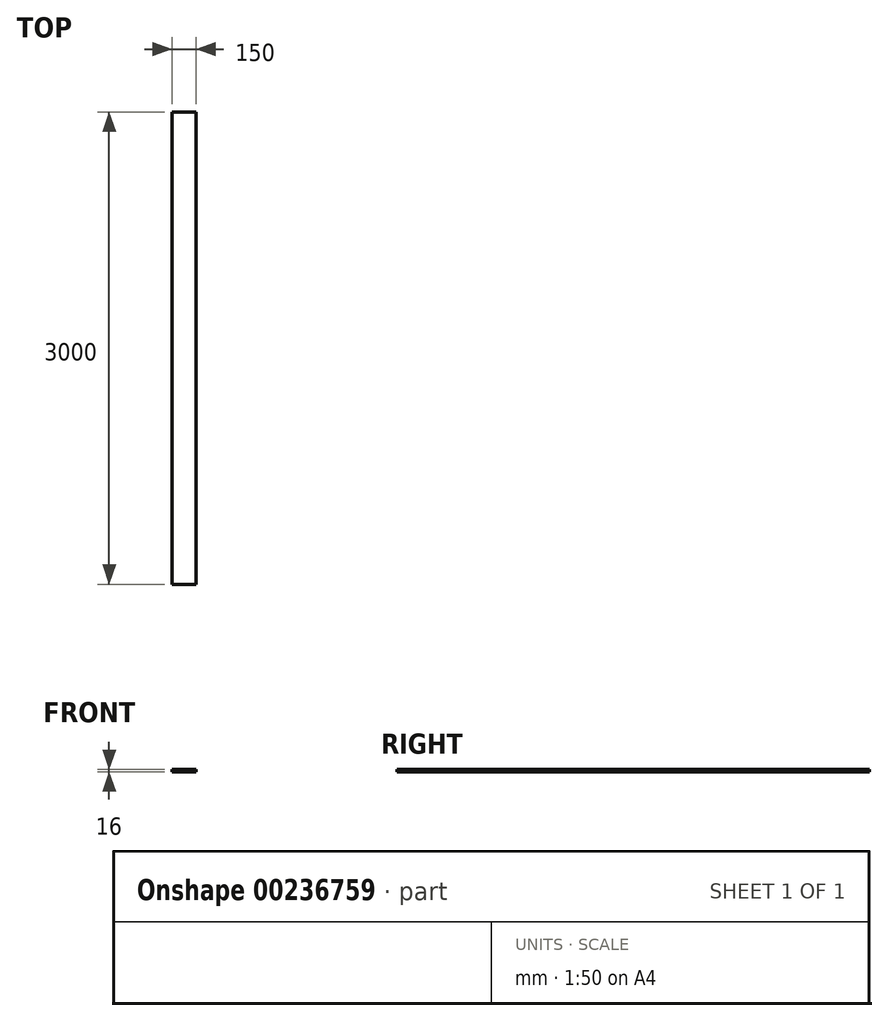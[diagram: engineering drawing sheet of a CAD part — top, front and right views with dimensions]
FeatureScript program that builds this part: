
annotation { "Feature Type Name" : "Feature", "Feature Type Description" : "" }
export const myFeature = defineFeature(function(context is Context, id is Id, definition is map)
    precondition{}
    {
        {
            var Q0;
            Q0=qCreatedBy(makeId("Front.planeOp"),FACE);
            var sketch = newSketch(context, id + "F0", { "sketchPlane" : qUnion([Q0])});
            skLineSegment(sketch, "E0.bottom", {"start": v(0, 0) * mm, "end": v(-150, 0) * mm});
            skLineSegment(sketch, "E0.top", {"start": v(0, 16) * mm, "end": v(-150, 16) * mm});
            skLineSegment(sketch, "E0.left", {"start": v(0, 0) * mm, "end": v(0, 16) * mm});
            skLineSegment(sketch, "E0.right", {"start": v(-150, 0) * mm, "end": v(-150, 16) * mm});
            skSolve(sketch);
        }
        {
            var Q0;
            Q0=makeQuery(id+"F0.imprint","IMPRINT",FACE,{"disambiguationData":[TD([[makeQuery(id+"F0.imprint","IMPRINT",EDGE,{"derivedFrom":sQuery(id+"F0.wireOp",EDGE,"E0.bottom")}),-1.0]])]});
            extrude(context, id + "F1", {"entities" : qUnion([Q0]), "oppositeDirection" : true, "depth" : 3000 * mm, "offsetDistance" : 25 * mm});
        }
    });
